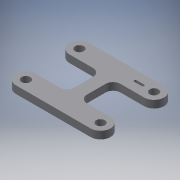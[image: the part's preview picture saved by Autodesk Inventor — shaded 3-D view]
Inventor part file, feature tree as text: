
AUTODESK INVENTOR PART (.ipt)
format: ipt  version: 2019 (Build 230136000, 136)  size: 155,136 bytes
history: native  units: mm
features: other x3, extrude x2, sketch x2, fillet x1, reference x1
ambient origin geometry x8: Origin, YZ Plane, XZ Plane, XY Plane, X Axis, Y Axis, Z Axis, Center Point
bodies: Body1 (feature_tree)
feature tree (9):
  other  "Твердое тело1"
  extrude  "Выдавливание1"  Depth=3.5mm
  fillet  "Сопряжение1"  Radius=21.5mm
  extrude  "Выдавливание2"  Depth=21.5mm
  sketch  "Эскиз1"
  sketch  "Эскиз2"
  reference  "Ссылка1"
  other  "Infrared sensor.iam"
  other  "Fastening:1"
